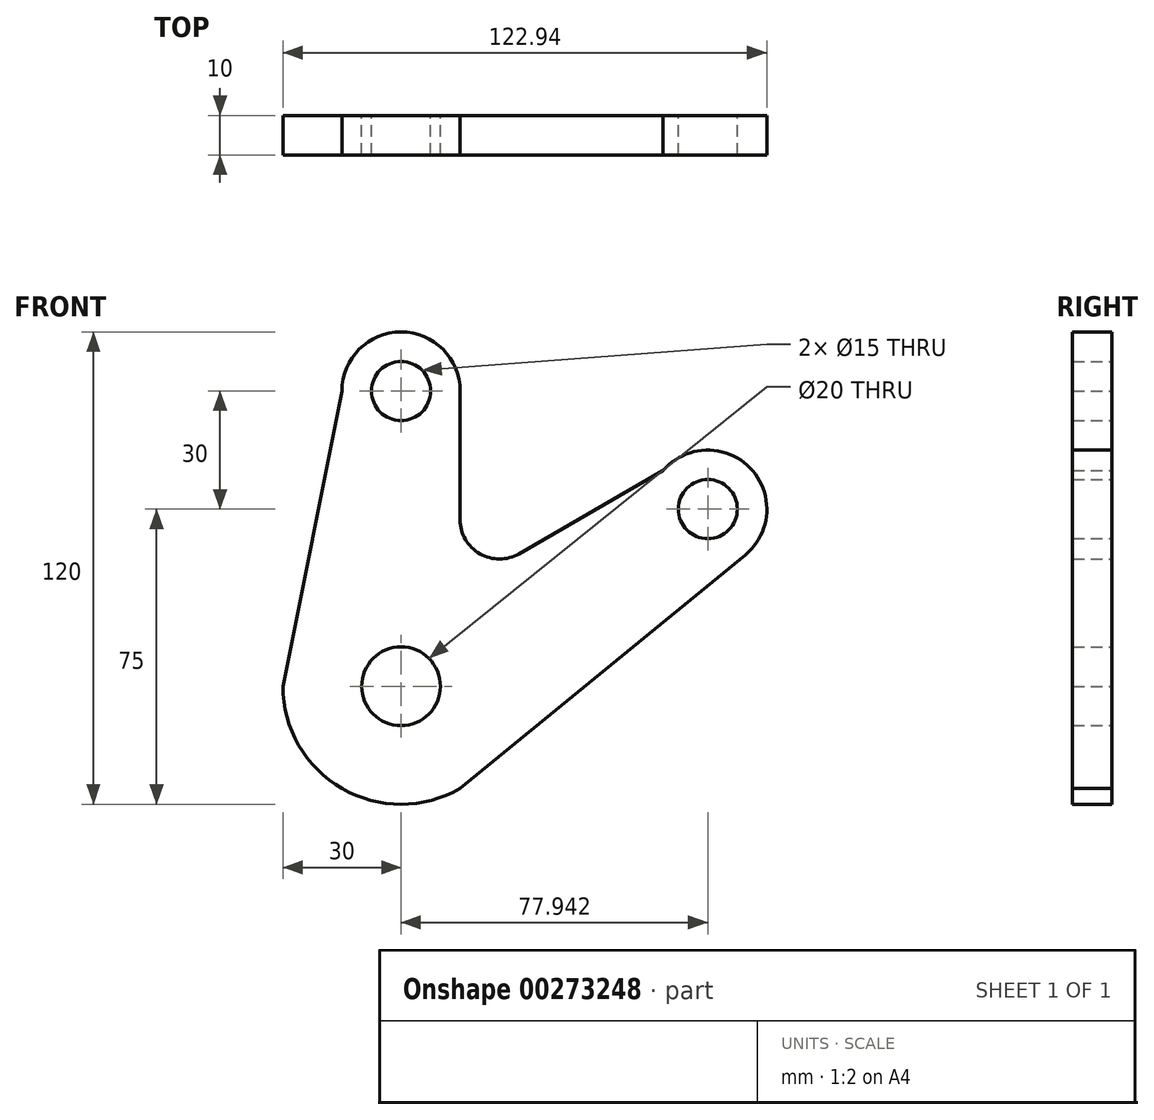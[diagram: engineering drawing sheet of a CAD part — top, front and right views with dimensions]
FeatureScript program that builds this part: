
annotation { "Feature Type Name" : "Feature", "Feature Type Description" : "" }
export const myFeature = defineFeature(function(context is Context, id is Id, definition is map)
    precondition{}
    {
        {
            var Q0;
            Q0=qCreatedBy(makeId("Front.planeOp"),FACE);
            var sketch = newSketch(context, id + "F0", { "sketchPlane" : qUnion([Q0])});
            skCircle(sketch, "E0", {"center": v(0, 0) * mm, "radius": 10 * mm});
            skCircle(sketch, "E1", {"center": v(0, 75) * mm, "radius": 7.5 * mm});
            skArc(sketch, "E2", {"start": v(15, 75) * mm, "mid": v(0, 90) * mm, "end": v(-15, 75) * mm});
            skLineSegment(sketch, "E3", {"start": v(15, 75) * mm, "end": v(15, 42.32) * mm});
            skLineSegment(sketch, "E4", {"start": v(30, 33.66) * mm, "end": v(66.56, 54.77) * mm});
            skPoint(sketch, "E5.visualSharp", {"position": v(15, 25) * mm});
            skArc(sketch, "E5.filletArc", {"start": v(15, 42.32) * mm, "mid": v(20, 33.66) * mm, "end": v(30, 33.66) * mm});
            skLineSegment(sketch, "E6", {"start": v(0, 0) * mm, "end": v(-64.59, 0) * mm, "construction": true});
            skLineSegment(sketch, "E7", {"start": v(0, 0) * mm, "end": v(31.56, -54.66) * mm, "construction": true});
            skArc(sketch, "E8", {"start": v(-30, 0) * mm, "mid": v(-15, -25.98) * mm, "end": v(15, -25.98) * mm});
            skLineSegment(sketch, "E9", {"start": v(-15, 75) * mm, "end": v(-30, 0) * mm});
            skLineSegment(sketch, "E10", {"start": v(15, -25.98) * mm, "end": v(87.45, 33.4) * mm});
            skCircle(sketch, "E11", {"center": v(77.94, 45) * mm, "radius": 7.5 * mm});
            skLineSegment(sketch, "E12", {"start": v(0, 75) * mm, "end": v(0, 0) * mm, "construction": true});
            skLineSegment(sketch, "E13", {"start": v(0, 0) * mm, "end": v(77.94, 45) * mm, "construction": true});
            skArc(sketch, "E14", {"start": v(87.45, 33.4) * mm, "mid": v(88.67, 55.49) * mm, "end": v(66.56, 54.77) * mm});
            skSolve(sketch);
        }
        {
            var Q0;
            Q0 = qSketchRegion(id + "F0", true);
            extrude(context, id + "F1", {"entities" : qUnion([Q0]), "depth" : 10 * mm});
        }
    });
